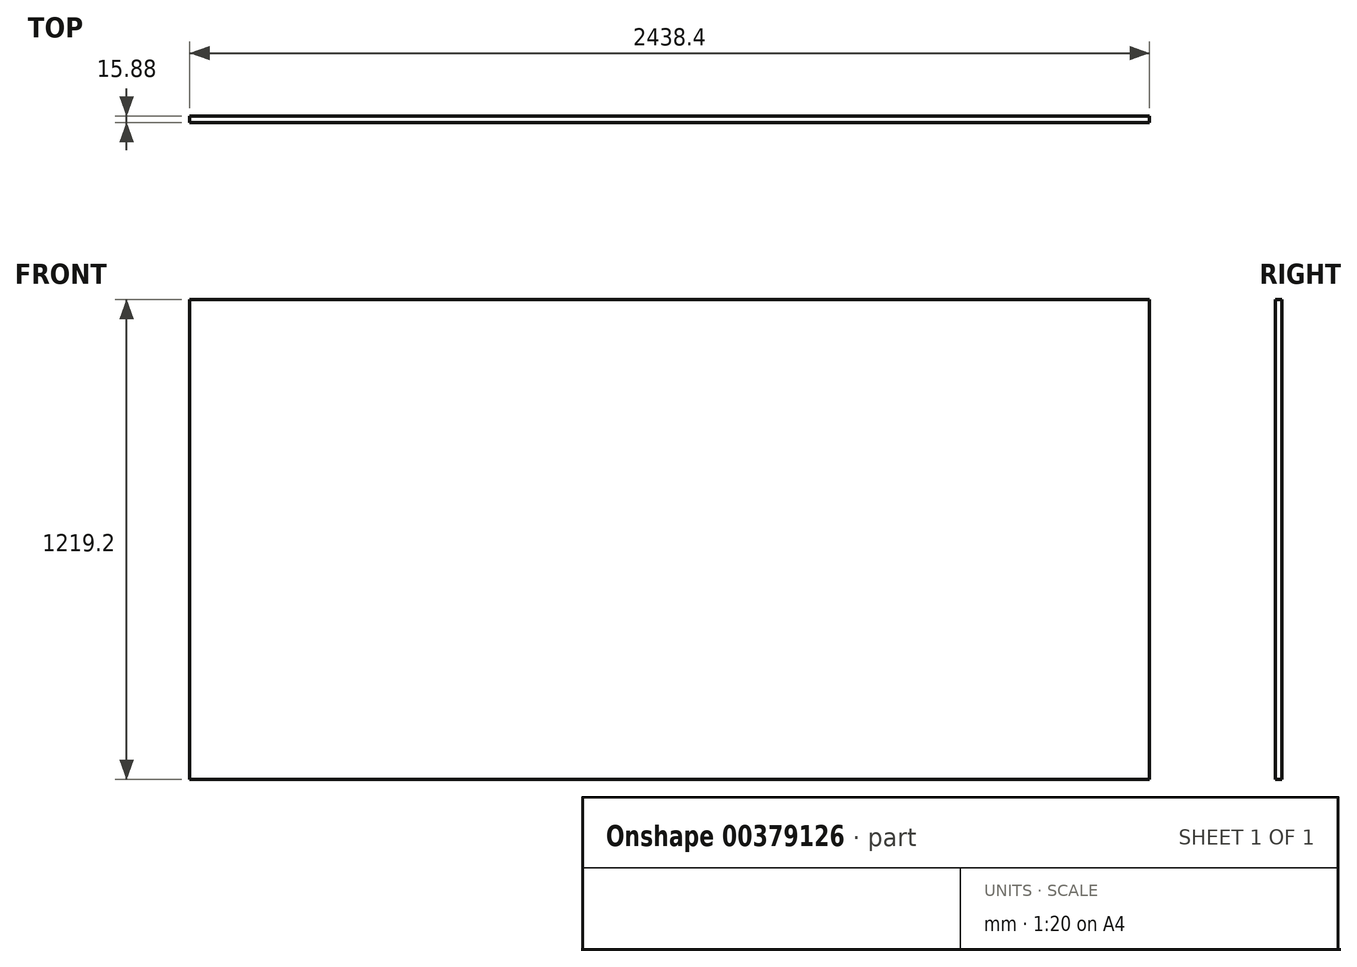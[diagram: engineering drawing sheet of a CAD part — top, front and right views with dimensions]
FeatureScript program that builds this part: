
annotation { "Feature Type Name" : "Feature", "Feature Type Description" : "" }
export const myFeature = defineFeature(function(context is Context, id is Id, definition is map)
    precondition{}
    {
        {
            var Q0;
            Q0=qCreatedBy(makeId("Front.planeOp"),FACE);
            var sketch = newSketch(context, id + "F0", { "sketchPlane" : qUnion([Q0])});
            skLineSegment(sketch, "E0.bottom", {"start": v(1219.2, 609.6) * mm, "end": v(-1219.2, 609.6) * mm});
            skLineSegment(sketch, "E0.top", {"start": v(1219.2, -609.6) * mm, "end": v(-1219.2, -609.6) * mm});
            skLineSegment(sketch, "E0.left", {"start": v(1219.2, 609.6) * mm, "end": v(1219.2, -609.6) * mm});
            skLineSegment(sketch, "E0.right", {"start": v(-1219.2, 609.6) * mm, "end": v(-1219.2, -609.6) * mm});
            skPoint(sketch, "E0.middle", {"position": v(0, 0) * mm});
            skSolve(sketch);
        }
        {
            var Q0;
            Q0=makeQuery(id+"F0.imprint","IMPRINT",FACE,{"disambiguationData":[TD([[makeQuery(id+"F0.imprint","IMPRINT",EDGE,{"derivedFrom":sQuery(id+"F0.wireOp",EDGE,"E0.bottom")}),1.0]])]});
            extrude(context, id + "F1", {"entities" : qUnion([Q0]), "depth" : 15.88 * mm});
        }
    });
